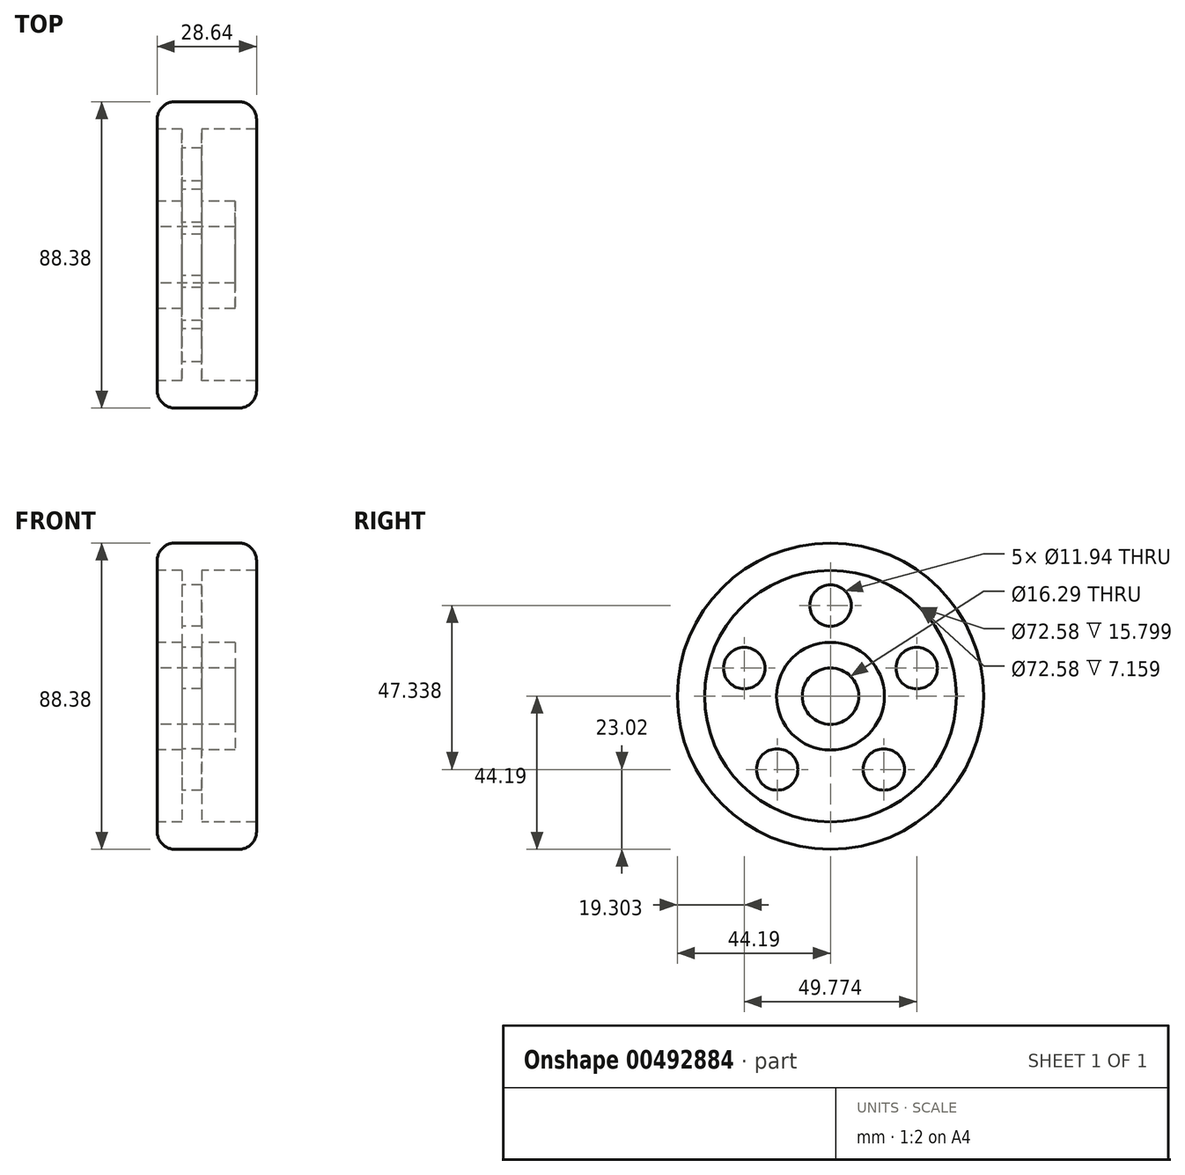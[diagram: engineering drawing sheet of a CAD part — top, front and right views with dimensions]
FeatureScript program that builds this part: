
annotation { "Feature Type Name" : "Feature", "Feature Type Description" : "" }
export const myFeature = defineFeature(function(context is Context, id is Id, definition is map)
    precondition{}
    {
        {
            var Q0;
            Q0=qCreatedBy(makeId("Front.planeOp"),FACE);
            var sketch = newSketch(context, id + "F0", { "sketchPlane" : qUnion([Q0])});
            skLineSegment(sketch, "E0", {"start": v(0, 15.55) * mm, "end": v(7.16, 15.55) * mm});
            skLineSegment(sketch, "E1", {"start": v(7.16, 15.55) * mm, "end": v(7.16, 36.29) * mm});
            skLineSegment(sketch, "E2", {"start": v(7.16, 36.29) * mm, "end": v(0, 36.29) * mm});
            skLineSegment(sketch, "E3", {"start": v(0, 36.29) * mm, "end": v(0, 44.19) * mm});
            skLineSegment(sketch, "E4", {"start": v(0, 44.19) * mm, "end": v(28.64, 44.19) * mm});
            skLineSegment(sketch, "E5", {"start": v(28.64, 44.19) * mm, "end": v(28.64, 36.29) * mm});
            skLineSegment(sketch, "E6", {"start": v(28.64, 36.29) * mm, "end": v(12.84, 36.29) * mm});
            skLineSegment(sketch, "E7", {"start": v(12.84, 36.29) * mm, "end": v(12.84, 15.55) * mm});
            skLineSegment(sketch, "E8", {"start": v(12.84, 15.55) * mm, "end": v(22.46, 15.55) * mm});
            skLineSegment(sketch, "E9", {"start": v(22.46, 15.55) * mm, "end": v(22.46, 8.15) * mm});
            skLineSegment(sketch, "E10", {"start": v(22.46, 8.15) * mm, "end": v(0, 8.15) * mm});
            skLineSegment(sketch, "E11", {"start": v(0, 8.15) * mm, "end": v(0, 15.55) * mm});
            skLineSegment(sketch, "E12", {"start": v(0, 0) * mm, "end": v(18.51, 0) * mm});
            skSolve(sketch);
        }
        {
            var Q0;
            Q0 = qSketchRegion(id + "F0", true);
            var Q1;
            Q1=sQuery(id+"F0.wireOp",EDGE,"E12");
            revolve(context, id + "F1", {"entities" : qUnion([Q0]), "axis" : qUnion([Q1]), "revolveType" : RevolveType.FULL});
        }
        {
            var Q0;
            Q0=makeQuery(id+"F1.opRevolve","SWEPT_FACE",FACE,{"disambiguationData":[OSD([sQuery(id+"F0.wireOp",EDGE,"E1")])]});
            var sketch = newSketch(context, id + "F2", { "sketchPlane" : qUnion([Q0])});
            skCircle(sketch, "E13", {"center": v(0, 26.17) * mm, "radius": 5.97 * mm});
            skCircle(sketch, "E14.1.0", {"center": v(-24.89, 8.09) * mm, "radius": 5.97 * mm});
            skCircle(sketch, "E14.2.0", {"center": v(-15.38, -21.17) * mm, "radius": 5.97 * mm});
            skCircle(sketch, "E14.3.0", {"center": v(15.38, -21.17) * mm, "radius": 5.97 * mm});
            skCircle(sketch, "E14.4.0", {"center": v(24.89, 8.09) * mm, "radius": 5.97 * mm});
            skPoint(sketch, "E14.center", {"position": v(0, 0) * mm});
            skSolve(sketch);
        }
        {
            var Q0;
            Q0=makeQuery(id+"F1.opRevolve","SWEPT_EDGE",EDGE,{"disambiguationData":[OSD([sQuery(id+"F0.wireOp",EDGE,"E4"),sQuery(id+"F0.wireOp",EDGE,"E5")])]});
            var Q1;
            Q1=makeQuery(id+"F1.opRevolve","SWEPT_EDGE",EDGE,{"disambiguationData":[OSD([sQuery(id+"F0.wireOp",EDGE,"E3"),sQuery(id+"F0.wireOp",EDGE,"E4")])]});
            fillet(context, id + "F3", {"entities" : qUnion([Q0, Q1]), "radius" : 5 * mm, "tangentPropagation" : true, "allowEdgeOverflow" : false});
        }
        {
            var Q0;
            Q0=makeQuery(id+"F2.imprint","IMPRINT",FACE,{"disambiguationData":[TD([[makeQuery(id+"F2.imprint","IMPRINT",EDGE,{"derivedFrom":sQuery(id+"F2.wireOp",EDGE,"E13")}),1.0]])]});
            var Q1;
            Q1=makeQuery(id+"F2.imprint","IMPRINT",FACE,{"disambiguationData":[TD([[makeQuery(id+"F2.imprint","IMPRINT",EDGE,{"derivedFrom":sQuery(id+"F2.wireOp",EDGE,"E14.1.0")}),1.0]])]});
            var Q2;
            Q2=makeQuery(id+"F2.imprint","IMPRINT",FACE,{"disambiguationData":[TD([[makeQuery(id+"F2.imprint","IMPRINT",EDGE,{"derivedFrom":sQuery(id+"F2.wireOp",EDGE,"E14.4.0")}),1.0]])]});
            var Q3;
            Q3=makeQuery(id+"F2.imprint","IMPRINT",FACE,{"disambiguationData":[TD([[makeQuery(id+"F2.imprint","IMPRINT",EDGE,{"derivedFrom":sQuery(id+"F2.wireOp",EDGE,"E14.2.0")}),1.0]])]});
            var Q4;
            Q4=makeQuery(id+"F2.imprint","IMPRINT",FACE,{"disambiguationData":[TD([[makeQuery(id+"F2.imprint","IMPRINT",EDGE,{"derivedFrom":sQuery(id+"F2.wireOp",EDGE,"E14.3.0")}),1.0]])]});
            extrude(context, id + "F4", {"entities" : qUnion([Q0, Q1, Q2, Q3, Q4]), "operationType" : NewBodyOperationType.REMOVE, "oppositeDirection" : true, "depth" : 25 * mm});
        }
    });
